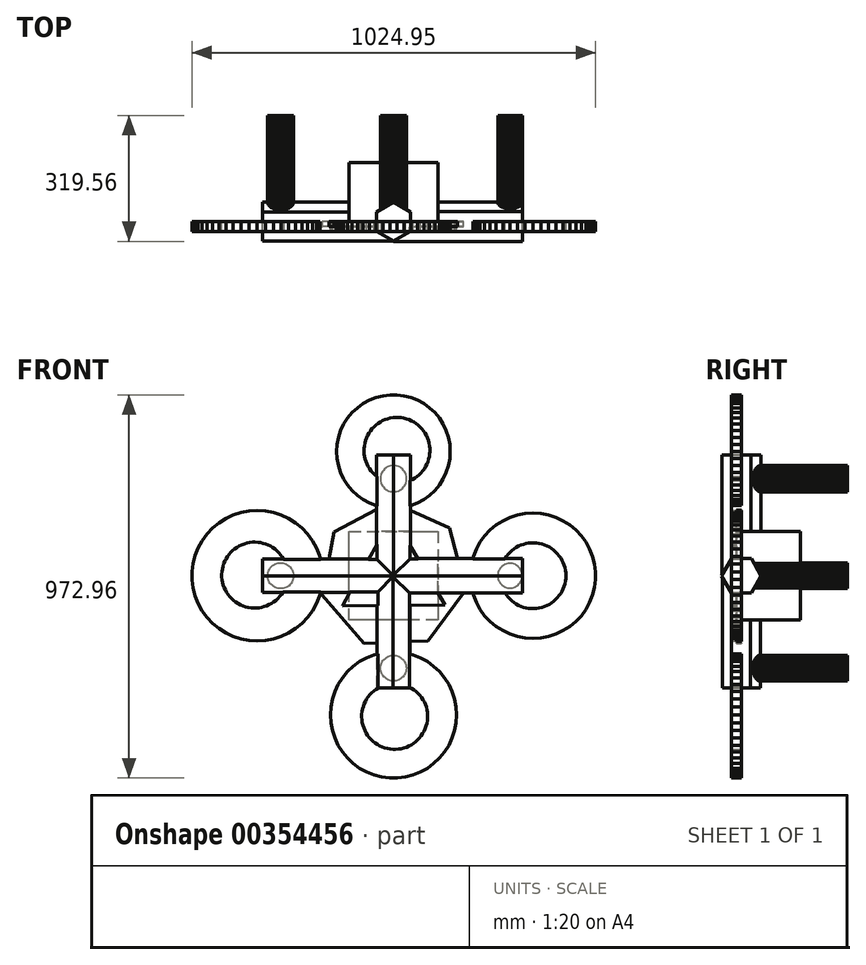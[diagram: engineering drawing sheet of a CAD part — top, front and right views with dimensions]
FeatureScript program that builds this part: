
annotation { "Feature Type Name" : "Feature", "Feature Type Description" : "" }
export const myFeature = defineFeature(function(context is Context, id is Id, definition is map)
    precondition{}
    {
        {
            var Q0;
            Q0=qCreatedBy(makeId("Front.planeOp"),FACE);
            var sketch = newSketch(context, id + "F0", { "sketchPlane" : qUnion([Q0])});
            skCircle(sketch, "E0.cCircle", {"center": v(0, 0) * mm, "radius": 75.35 * mm, "construction": true});
            skLineSegment(sketch, "E0.0", {"start": v(-129.73, -76.68) * mm, "end": v(-1.54, 150.7) * mm});
            skLineSegment(sketch, "E0.1", {"start": v(-1.54, 150.7) * mm, "end": v(131.28, -74.01) * mm});
            skLineSegment(sketch, "E0.2", {"start": v(131.28, -74.01) * mm, "end": v(-129.73, -76.68) * mm});
            skPoint(sketch, "E0.0.midPoint", {"position": v(-65.64, 37) * mm});
            skSolve(sketch);
        }
        {
            var Q0;
            Q0=makeQuery(id+"F0.imprint","IMPRINT",FACE,{"disambiguationData":[TD([[makeQuery(id+"F0.imprint","IMPRINT",EDGE,{"derivedFrom":sQuery(id+"F0.wireOp",EDGE,"E0.0")}),-1.0]])]});
            extrude(context, id + "F1", {"entities" : qUnion([Q0]), "depth" : 25.4 * mm});
        }
        {
            var Q0;
            Q0=qCreatedBy(makeId("Front.planeOp"),FACE);
            var sketch = newSketch(context, id + "F2", { "sketchPlane" : qUnion([Q0])});
            skCircle(sketch, "E1.cCircle", {"center": v(0, 0) * mm, "radius": 168.77 * mm, "construction": true});
            skLineSegment(sketch, "E1.0", {"start": v(-150.57, 111.44) * mm, "end": v(-6.75, 187.2) * mm});
            skLineSegment(sketch, "E1.1", {"start": v(-6.75, 187.2) * mm, "end": v(142.15, 122) * mm});
            skLineSegment(sketch, "E1.2", {"start": v(142.15, 122) * mm, "end": v(184.01, -35.08) * mm});
            skLineSegment(sketch, "E1.3", {"start": v(184.01, -35.08) * mm, "end": v(87.3, -165.74) * mm});
            skLineSegment(sketch, "E1.4", {"start": v(87.3, -165.74) * mm, "end": v(-75.14, -171.6) * mm});
            skLineSegment(sketch, "E1.5", {"start": v(-75.14, -171.6) * mm, "end": v(-181, -48.24) * mm});
            skLineSegment(sketch, "E1.6", {"start": v(-181, -48.24) * mm, "end": v(-150.57, 111.44) * mm});
            skPoint(sketch, "E1.0.midPoint", {"position": v(-78.66, 149.32) * mm});
            skSolve(sketch);
        }
        {
            var Q0;
            Q0=makeQuery(id+"F2.imprint","IMPRINT",FACE,{"disambiguationData":[TD([[makeQuery(id+"F2.imprint","IMPRINT",EDGE,{"derivedFrom":sQuery(id+"F2.wireOp",EDGE,"E1.0")}),-1.0]])]});
            extrude(context, id + "F3", {"entities" : qUnion([Q0]), "operationType" : NewBodyOperationType.ADD, "depth" : 12.95 * mm});
        }
        {
            var Q0;
            Q0=qCreatedBy(makeId("Right.planeOp"),FACE);
            var sketch = newSketch(context, id + "F4", { "sketchPlane" : qUnion([Q0])});
            skCircle(sketch, "E2.cCircle", {"center": v(0, 0) * mm, "radius": 43.58 * mm, "construction": true});
            skLineSegment(sketch, "E2.0", {"start": v(25.16, -43.58) * mm, "end": v(-25.16, -43.58) * mm});
            skLineSegment(sketch, "E2.1", {"start": v(-25.16, -43.58) * mm, "end": v(-50.32, 0) * mm});
            skLineSegment(sketch, "E2.2", {"start": v(-50.32, 0) * mm, "end": v(-25.16, 43.58) * mm});
            skLineSegment(sketch, "E2.3", {"start": v(-25.16, 43.58) * mm, "end": v(25.16, 43.58) * mm});
            skLineSegment(sketch, "E2.4", {"start": v(25.16, 43.58) * mm, "end": v(50.32, 0) * mm});
            skLineSegment(sketch, "E2.5", {"start": v(50.32, 0) * mm, "end": v(25.16, -43.58) * mm});
            skPoint(sketch, "E2.0.midPoint", {"position": v(0, -43.58) * mm});
            skSolve(sketch);
        }
        {
            var Q0;
            Q0 = qSketchRegion(id + "F4", true);
            extrude(context, id + "F5", {"entities" : qUnion([Q0]), "operationType" : NewBodyOperationType.ADD, "depth" : 327.66 * mm});
        }
        {
            var Q0;
            Q0=qCreatedBy(makeId("Right.planeOp"),FACE);
            var sketch = newSketch(context, id + "F6", { "sketchPlane" : qUnion([Q0])});
            skCircle(sketch, "E3.cCircle", {"center": v(0, 0) * mm, "radius": 42.73 * mm, "construction": true});
            skLineSegment(sketch, "E3.0", {"start": v(-49.35, 0.04) * mm, "end": v(-24.64, 42.76) * mm});
            skLineSegment(sketch, "E3.1", {"start": v(-24.64, 42.76) * mm, "end": v(24.7, 42.71) * mm});
            skLineSegment(sketch, "E3.2", {"start": v(24.7, 42.71) * mm, "end": v(49.35, -0.04) * mm});
            skLineSegment(sketch, "E3.3", {"start": v(49.35, -0.04) * mm, "end": v(24.64, -42.76) * mm});
            skLineSegment(sketch, "E3.4", {"start": v(24.64, -42.76) * mm, "end": v(-24.7, -42.71) * mm});
            skLineSegment(sketch, "E3.5", {"start": v(-24.7, -42.71) * mm, "end": v(-49.35, 0.04) * mm});
            skPoint(sketch, "E3.0.midPoint", {"position": v(-37, 21.4) * mm});
            skSolve(sketch);
        }
        {
            var Q0;
            Q0 = qSketchRegion(id + "F6", true);
            extrude(context, id + "F7", {"entities" : qUnion([Q0]), "operationType" : NewBodyOperationType.ADD, "oppositeDirection" : true, "depth" : 332.74 * mm});
        }
        {
            var Q0;
            Q0=qCreatedBy(makeId("Top.planeOp"),FACE);
            var sketch = newSketch(context, id + "F8", { "sketchPlane" : qUnion([Q0])});
            skCircle(sketch, "E4.cCircle", {"center": v(0, 0) * mm, "radius": 42.9 * mm, "construction": true});
            skLineSegment(sketch, "E4.0", {"start": v(-42.9, -24.77) * mm, "end": v(-42.9, 24.77) * mm});
            skLineSegment(sketch, "E4.1", {"start": v(-42.9, 24.77) * mm, "end": v(0, 49.53) * mm});
            skLineSegment(sketch, "E4.2", {"start": v(0, 49.53) * mm, "end": v(42.9, 24.77) * mm});
            skLineSegment(sketch, "E4.3", {"start": v(42.9, 24.77) * mm, "end": v(42.9, -24.77) * mm});
            skLineSegment(sketch, "E4.4", {"start": v(42.9, -24.77) * mm, "end": v(0, -49.53) * mm});
            skLineSegment(sketch, "E4.5", {"start": v(0, -49.53) * mm, "end": v(-42.9, -24.77) * mm});
            skPoint(sketch, "E4.0.midPoint", {"position": v(-42.9, 0) * mm});
            skSolve(sketch);
        }
        {
            var Q0;
            Q0 = qSketchRegion(id + "F8", true);
            extrude(context, id + "F9", {"entities" : qUnion([Q0]), "operationType" : NewBodyOperationType.ADD, "depth" : 307.34 * mm});
        }
        {
            var Q0;
            Q0=qCreatedBy(makeId("Top.planeOp"),FACE);
            var sketch = newSketch(context, id + "F10", { "sketchPlane" : qUnion([Q0])});
            skCircle(sketch, "E5.cCircle", {"center": v(0, 0) * mm, "radius": 41.69 * mm, "construction": true});
            skLineSegment(sketch, "E5.0", {"start": v(-0.86, -48.13) * mm, "end": v(-42.11, -23.32) * mm});
            skLineSegment(sketch, "E5.1", {"start": v(-42.11, -23.32) * mm, "end": v(-41.25, 24.81) * mm});
            skLineSegment(sketch, "E5.2", {"start": v(-41.25, 24.81) * mm, "end": v(0.86, 48.13) * mm});
            skLineSegment(sketch, "E5.3", {"start": v(0.86, 48.13) * mm, "end": v(42.11, 23.32) * mm});
            skLineSegment(sketch, "E5.4", {"start": v(42.11, 23.32) * mm, "end": v(41.25, -24.81) * mm});
            skLineSegment(sketch, "E5.5", {"start": v(41.25, -24.81) * mm, "end": v(-0.86, -48.13) * mm});
            skPoint(sketch, "E5.0.midPoint", {"position": v(-21.49, -35.72) * mm});
            skSolve(sketch);
        }
        {
            var Q0;
            Q0 = qSketchRegion(id + "F10", true);
            extrude(context, id + "F11", {"entities" : qUnion([Q0]), "operationType" : NewBodyOperationType.ADD, "oppositeDirection" : true, "depth" : 284.48 * mm});
        }
        {
            var Q0;
            Q0=qCreatedBy(makeId("Front.planeOp"),FACE);
            var sketch = newSketch(context, id + "F12", { "sketchPlane" : qUnion([Q0])});
            skCircle(sketch, "E6.cCircle", {"center": v(0, 315.57) * mm, "radius": 143.82 * mm, "construction": true});
            skLineSegment(sketch, "E6.0", {"start": v(-9.05, 459.4) * mm, "end": v(9.05, 459.4) * mm});
            skLineSegment(sketch, "E6.1", {"start": v(9.05, 459.4) * mm, "end": v(27, 457.13) * mm});
            skLineSegment(sketch, "E6.2", {"start": v(27, 457.13) * mm, "end": v(44.53, 452.63) * mm});
            skLineSegment(sketch, "E6.3", {"start": v(44.53, 452.63) * mm, "end": v(61.36, 445.96) * mm});
            skLineSegment(sketch, "E6.4", {"start": v(61.36, 445.96) * mm, "end": v(77.22, 437.25) * mm});
            skLineSegment(sketch, "E6.5", {"start": v(77.22, 437.25) * mm, "end": v(91.86, 426.6) * mm});
            skLineSegment(sketch, "E6.6", {"start": v(91.86, 426.6) * mm, "end": v(105.05, 414.22) * mm});
            skLineSegment(sketch, "E6.7", {"start": v(105.05, 414.22) * mm, "end": v(116.58, 400.28) * mm});
            skLineSegment(sketch, "E6.8", {"start": v(116.58, 400.28) * mm, "end": v(126.28, 385) * mm});
            skLineSegment(sketch, "E6.9", {"start": v(126.28, 385) * mm, "end": v(133.99, 368.62) * mm});
            skLineSegment(sketch, "E6.10", {"start": v(133.99, 368.62) * mm, "end": v(139.58, 351.41) * mm});
            skLineSegment(sketch, "E6.11", {"start": v(139.58, 351.41) * mm, "end": v(142.97, 333.63) * mm});
            skLineSegment(sketch, "E6.12", {"start": v(142.97, 333.63) * mm, "end": v(144.1, 315.57) * mm});
            skLineSegment(sketch, "E6.13", {"start": v(144.1, 315.57) * mm, "end": v(142.97, 297.51) * mm});
            skLineSegment(sketch, "E6.14", {"start": v(142.97, 297.51) * mm, "end": v(139.58, 279.74) * mm});
            skLineSegment(sketch, "E6.15", {"start": v(139.58, 279.74) * mm, "end": v(133.99, 262.52) * mm});
            skLineSegment(sketch, "E6.16", {"start": v(133.99, 262.52) * mm, "end": v(126.28, 246.15) * mm});
            skLineSegment(sketch, "E6.17", {"start": v(126.28, 246.15) * mm, "end": v(116.58, 230.87) * mm});
            skLineSegment(sketch, "E6.18", {"start": v(116.58, 230.87) * mm, "end": v(105.05, 216.93) * mm});
            skLineSegment(sketch, "E6.19", {"start": v(105.05, 216.93) * mm, "end": v(91.86, 204.54) * mm});
            skLineSegment(sketch, "E6.20", {"start": v(91.86, 204.54) * mm, "end": v(77.22, 193.9) * mm});
            skLineSegment(sketch, "E6.21", {"start": v(77.22, 193.9) * mm, "end": v(61.36, 185.18) * mm});
            skLineSegment(sketch, "E6.22", {"start": v(61.36, 185.18) * mm, "end": v(44.53, 178.52) * mm});
            skLineSegment(sketch, "E6.23", {"start": v(44.53, 178.52) * mm, "end": v(27, 174.02) * mm});
            skLineSegment(sketch, "E6.24", {"start": v(27, 174.02) * mm, "end": v(9.05, 171.75) * mm});
            skLineSegment(sketch, "E6.25", {"start": v(9.05, 171.75) * mm, "end": v(-9.05, 171.75) * mm});
            skLineSegment(sketch, "E6.26", {"start": v(-9.05, 171.75) * mm, "end": v(-27, 174.02) * mm});
            skLineSegment(sketch, "E6.27", {"start": v(-27, 174.02) * mm, "end": v(-44.53, 178.52) * mm});
            skLineSegment(sketch, "E6.28", {"start": v(-44.53, 178.52) * mm, "end": v(-61.36, 185.18) * mm});
            skLineSegment(sketch, "E6.29", {"start": v(-61.36, 185.18) * mm, "end": v(-77.22, 193.9) * mm});
            skLineSegment(sketch, "E6.30", {"start": v(-77.22, 193.9) * mm, "end": v(-91.86, 204.54) * mm});
            skLineSegment(sketch, "E6.31", {"start": v(-91.86, 204.54) * mm, "end": v(-105.05, 216.93) * mm});
            skLineSegment(sketch, "E6.32", {"start": v(-105.05, 216.93) * mm, "end": v(-116.58, 230.87) * mm});
            skLineSegment(sketch, "E6.33", {"start": v(-116.58, 230.87) * mm, "end": v(-126.28, 246.15) * mm});
            skLineSegment(sketch, "E6.34", {"start": v(-126.28, 246.15) * mm, "end": v(-133.99, 262.52) * mm});
            skLineSegment(sketch, "E6.35", {"start": v(-133.99, 262.52) * mm, "end": v(-139.58, 279.74) * mm});
            skLineSegment(sketch, "E6.36", {"start": v(-139.58, 279.74) * mm, "end": v(-142.97, 297.51) * mm});
            skLineSegment(sketch, "E6.37", {"start": v(-142.97, 297.51) * mm, "end": v(-144.1, 315.57) * mm});
            skLineSegment(sketch, "E6.38", {"start": v(-144.1, 315.57) * mm, "end": v(-142.97, 333.63) * mm});
            skLineSegment(sketch, "E6.39", {"start": v(-142.97, 333.63) * mm, "end": v(-139.58, 351.41) * mm});
            skLineSegment(sketch, "E6.40", {"start": v(-139.58, 351.41) * mm, "end": v(-133.99, 368.62) * mm});
            skLineSegment(sketch, "E6.41", {"start": v(-133.99, 368.62) * mm, "end": v(-126.28, 385) * mm});
            skLineSegment(sketch, "E6.42", {"start": v(-126.28, 385) * mm, "end": v(-116.58, 400.28) * mm});
            skLineSegment(sketch, "E6.43", {"start": v(-116.58, 400.28) * mm, "end": v(-105.05, 414.22) * mm});
            skLineSegment(sketch, "E6.44", {"start": v(-105.05, 414.22) * mm, "end": v(-91.86, 426.6) * mm});
            skLineSegment(sketch, "E6.45", {"start": v(-91.86, 426.6) * mm, "end": v(-77.22, 437.25) * mm});
            skLineSegment(sketch, "E6.46", {"start": v(-77.22, 437.25) * mm, "end": v(-61.36, 445.96) * mm});
            skLineSegment(sketch, "E6.47", {"start": v(-61.36, 445.96) * mm, "end": v(-44.53, 452.63) * mm});
            skLineSegment(sketch, "E6.48", {"start": v(-44.53, 452.63) * mm, "end": v(-27, 457.13) * mm});
            skLineSegment(sketch, "E6.49", {"start": v(-27, 457.13) * mm, "end": v(-9.05, 459.4) * mm});
            skPoint(sketch, "E6.0.midPoint", {"position": v(0, 459.4) * mm});
            skCircle(sketch, "E7.cCircle", {"center": v(354.48, 0) * mm, "radius": 158.96 * mm, "construction": true});
            skLineSegment(sketch, "E7.0", {"start": v(513.44, 10) * mm, "end": v(513.44, -10) * mm});
            skLineSegment(sketch, "E7.1", {"start": v(513.44, -10) * mm, "end": v(510.94, -29.85) * mm});
            skLineSegment(sketch, "E7.2", {"start": v(510.94, -29.85) * mm, "end": v(505.96, -49.22) * mm});
            skLineSegment(sketch, "E7.3", {"start": v(505.96, -49.22) * mm, "end": v(498.6, -67.82) * mm});
            skLineSegment(sketch, "E7.4", {"start": v(498.6, -67.82) * mm, "end": v(488.96, -85.34) * mm});
            skLineSegment(sketch, "E7.5", {"start": v(488.96, -85.34) * mm, "end": v(477.2, -101.53) * mm});
            skLineSegment(sketch, "E7.6", {"start": v(477.2, -101.53) * mm, "end": v(463.51, -116.1) * mm});
            skLineSegment(sketch, "E7.7", {"start": v(463.51, -116.1) * mm, "end": v(448.1, -128.86) * mm});
            skLineSegment(sketch, "E7.8", {"start": v(448.1, -128.86) * mm, "end": v(431.21, -139.57) * mm});
            skLineSegment(sketch, "E7.9", {"start": v(431.21, -139.57) * mm, "end": v(413.12, -148.1) * mm});
            skLineSegment(sketch, "E7.10", {"start": v(413.12, -148.1) * mm, "end": v(394.1, -154.27) * mm});
            skLineSegment(sketch, "E7.11", {"start": v(394.1, -154.27) * mm, "end": v(374.44, -158.02) * mm});
            skLineSegment(sketch, "E7.12", {"start": v(374.44, -158.02) * mm, "end": v(354.48, -159.28) * mm});
            skLineSegment(sketch, "E7.13", {"start": v(354.48, -159.28) * mm, "end": v(334.52, -158.02) * mm});
            skLineSegment(sketch, "E7.14", {"start": v(334.52, -158.02) * mm, "end": v(314.87, -154.27) * mm});
            skLineSegment(sketch, "E7.15", {"start": v(314.87, -154.27) * mm, "end": v(295.85, -148.1) * mm});
            skLineSegment(sketch, "E7.16", {"start": v(295.85, -148.1) * mm, "end": v(277.75, -139.57) * mm});
            skLineSegment(sketch, "E7.17", {"start": v(277.75, -139.57) * mm, "end": v(260.86, -128.86) * mm});
            skLineSegment(sketch, "E7.18", {"start": v(260.86, -128.86) * mm, "end": v(245.45, -116.1) * mm});
            skLineSegment(sketch, "E7.19", {"start": v(245.45, -116.1) * mm, "end": v(231.76, -101.53) * mm});
            skLineSegment(sketch, "E7.20", {"start": v(231.76, -101.53) * mm, "end": v(220, -85.34) * mm});
            skLineSegment(sketch, "E7.21", {"start": v(220, -85.34) * mm, "end": v(210.36, -67.82) * mm});
            skLineSegment(sketch, "E7.22", {"start": v(210.36, -67.82) * mm, "end": v(203, -49.22) * mm});
            skLineSegment(sketch, "E7.23", {"start": v(203, -49.22) * mm, "end": v(198.03, -29.85) * mm});
            skLineSegment(sketch, "E7.24", {"start": v(198.03, -29.85) * mm, "end": v(195.52, -10) * mm});
            skLineSegment(sketch, "E7.25", {"start": v(195.52, -10) * mm, "end": v(195.52, 10) * mm});
            skLineSegment(sketch, "E7.26", {"start": v(195.52, 10) * mm, "end": v(198.03, 29.85) * mm});
            skLineSegment(sketch, "E7.27", {"start": v(198.03, 29.85) * mm, "end": v(203, 49.22) * mm});
            skLineSegment(sketch, "E7.28", {"start": v(203, 49.22) * mm, "end": v(210.36, 67.82) * mm});
            skLineSegment(sketch, "E7.29", {"start": v(210.36, 67.82) * mm, "end": v(220, 85.34) * mm});
            skLineSegment(sketch, "E7.30", {"start": v(220, 85.34) * mm, "end": v(231.76, 101.53) * mm});
            skLineSegment(sketch, "E7.31", {"start": v(231.76, 101.53) * mm, "end": v(245.45, 116.1) * mm});
            skLineSegment(sketch, "E7.32", {"start": v(245.45, 116.1) * mm, "end": v(260.86, 128.86) * mm});
            skLineSegment(sketch, "E7.33", {"start": v(260.86, 128.86) * mm, "end": v(277.75, 139.57) * mm});
            skLineSegment(sketch, "E7.34", {"start": v(277.75, 139.57) * mm, "end": v(295.85, 148.1) * mm});
            skLineSegment(sketch, "E7.35", {"start": v(295.85, 148.1) * mm, "end": v(314.87, 154.27) * mm});
            skLineSegment(sketch, "E7.36", {"start": v(314.87, 154.27) * mm, "end": v(334.52, 158.02) * mm});
            skLineSegment(sketch, "E7.37", {"start": v(334.52, 158.02) * mm, "end": v(354.48, 159.28) * mm});
            skLineSegment(sketch, "E7.38", {"start": v(354.48, 159.28) * mm, "end": v(374.44, 158.02) * mm});
            skLineSegment(sketch, "E7.39", {"start": v(374.44, 158.02) * mm, "end": v(394.1, 154.27) * mm});
            skLineSegment(sketch, "E7.40", {"start": v(394.1, 154.27) * mm, "end": v(413.12, 148.1) * mm});
            skLineSegment(sketch, "E7.41", {"start": v(413.12, 148.1) * mm, "end": v(431.21, 139.57) * mm});
            skLineSegment(sketch, "E7.42", {"start": v(431.21, 139.57) * mm, "end": v(448.1, 128.86) * mm});
            skLineSegment(sketch, "E7.43", {"start": v(448.1, 128.86) * mm, "end": v(463.51, 116.1) * mm});
            skLineSegment(sketch, "E7.44", {"start": v(463.51, 116.1) * mm, "end": v(477.2, 101.53) * mm});
            skLineSegment(sketch, "E7.45", {"start": v(477.2, 101.53) * mm, "end": v(488.96, 85.34) * mm});
            skLineSegment(sketch, "E7.46", {"start": v(488.96, 85.34) * mm, "end": v(498.6, 67.82) * mm});
            skLineSegment(sketch, "E7.47", {"start": v(498.6, 67.82) * mm, "end": v(505.96, 49.22) * mm});
            skLineSegment(sketch, "E7.48", {"start": v(505.96, 49.22) * mm, "end": v(510.94, 29.85) * mm});
            skLineSegment(sketch, "E7.49", {"start": v(510.94, 29.85) * mm, "end": v(513.44, 10) * mm});
            skPoint(sketch, "E7.0.midPoint", {"position": v(513.44, 0) * mm});
            skCircle(sketch, "E8.cCircle", {"center": v(-346.01, 0) * mm, "radius": 165.5 * mm, "construction": true});
            skLineSegment(sketch, "E8.0", {"start": v(-511.5, -10.41) * mm, "end": v(-511.5, 10.41) * mm});
            skLineSegment(sketch, "E8.1", {"start": v(-511.5, 10.41) * mm, "end": v(-508.9, 31.07) * mm});
            skLineSegment(sketch, "E8.2", {"start": v(-508.9, 31.07) * mm, "end": v(-503.72, 51.24) * mm});
            skLineSegment(sketch, "E8.3", {"start": v(-503.72, 51.24) * mm, "end": v(-496.05, 70.6) * mm});
            skLineSegment(sketch, "E8.4", {"start": v(-496.05, 70.6) * mm, "end": v(-486.02, 88.85) * mm});
            skLineSegment(sketch, "E8.5", {"start": v(-486.02, 88.85) * mm, "end": v(-473.78, 105.7) * mm});
            skLineSegment(sketch, "E8.6", {"start": v(-473.78, 105.7) * mm, "end": v(-459.53, 120.88) * mm});
            skLineSegment(sketch, "E8.7", {"start": v(-459.53, 120.88) * mm, "end": v(-443.48, 134.15) * mm});
            skLineSegment(sketch, "E8.8", {"start": v(-443.48, 134.15) * mm, "end": v(-425.9, 145.31) * mm});
            skLineSegment(sketch, "E8.9", {"start": v(-425.9, 145.31) * mm, "end": v(-407.06, 154.18) * mm});
            skLineSegment(sketch, "E8.10", {"start": v(-407.06, 154.18) * mm, "end": v(-387.25, 160.61) * mm});
            skLineSegment(sketch, "E8.11", {"start": v(-387.25, 160.61) * mm, "end": v(-366.8, 164.52) * mm});
            skLineSegment(sketch, "E8.12", {"start": v(-366.8, 164.52) * mm, "end": v(-346.01, 165.82) * mm});
            skLineSegment(sketch, "E8.13", {"start": v(-346.01, 165.82) * mm, "end": v(-325.23, 164.52) * mm});
            skLineSegment(sketch, "E8.14", {"start": v(-325.23, 164.52) * mm, "end": v(-304.78, 160.61) * mm});
            skLineSegment(sketch, "E8.15", {"start": v(-304.78, 160.61) * mm, "end": v(-284.97, 154.18) * mm});
            skLineSegment(sketch, "E8.16", {"start": v(-284.97, 154.18) * mm, "end": v(-266.13, 145.31) * mm});
            skLineSegment(sketch, "E8.17", {"start": v(-266.13, 145.31) * mm, "end": v(-248.55, 134.15) * mm});
            skLineSegment(sketch, "E8.18", {"start": v(-248.55, 134.15) * mm, "end": v(-232.5, 120.88) * mm});
            skLineSegment(sketch, "E8.19", {"start": v(-232.5, 120.88) * mm, "end": v(-218.25, 105.7) * mm});
            skLineSegment(sketch, "E8.20", {"start": v(-218.25, 105.7) * mm, "end": v(-206, 88.85) * mm});
            skLineSegment(sketch, "E8.21", {"start": v(-206, 88.85) * mm, "end": v(-195.97, 70.6) * mm});
            skLineSegment(sketch, "E8.22", {"start": v(-195.97, 70.6) * mm, "end": v(-188.3, 51.24) * mm});
            skLineSegment(sketch, "E8.23", {"start": v(-188.3, 51.24) * mm, "end": v(-183.13, 31.07) * mm});
            skLineSegment(sketch, "E8.24", {"start": v(-183.13, 31.07) * mm, "end": v(-180.52, 10.41) * mm});
            skLineSegment(sketch, "E8.25", {"start": v(-180.52, 10.41) * mm, "end": v(-180.52, -10.41) * mm});
            skLineSegment(sketch, "E8.26", {"start": v(-180.52, -10.41) * mm, "end": v(-183.13, -31.07) * mm});
            skLineSegment(sketch, "E8.27", {"start": v(-183.13, -31.07) * mm, "end": v(-188.3, -51.24) * mm});
            skLineSegment(sketch, "E8.28", {"start": v(-188.3, -51.24) * mm, "end": v(-195.97, -70.6) * mm});
            skLineSegment(sketch, "E8.29", {"start": v(-195.97, -70.6) * mm, "end": v(-206, -88.85) * mm});
            skLineSegment(sketch, "E8.30", {"start": v(-206, -88.85) * mm, "end": v(-218.25, -105.7) * mm});
            skLineSegment(sketch, "E8.31", {"start": v(-218.25, -105.7) * mm, "end": v(-232.5, -120.88) * mm});
            skLineSegment(sketch, "E8.32", {"start": v(-232.5, -120.88) * mm, "end": v(-248.55, -134.15) * mm});
            skLineSegment(sketch, "E8.33", {"start": v(-248.55, -134.15) * mm, "end": v(-266.13, -145.31) * mm});
            skLineSegment(sketch, "E8.34", {"start": v(-266.13, -145.31) * mm, "end": v(-284.97, -154.18) * mm});
            skLineSegment(sketch, "E8.35", {"start": v(-284.97, -154.18) * mm, "end": v(-304.78, -160.61) * mm});
            skLineSegment(sketch, "E8.36", {"start": v(-304.78, -160.61) * mm, "end": v(-325.23, -164.52) * mm});
            skLineSegment(sketch, "E8.37", {"start": v(-325.23, -164.52) * mm, "end": v(-346.01, -165.82) * mm});
            skLineSegment(sketch, "E8.38", {"start": v(-346.01, -165.82) * mm, "end": v(-366.8, -164.52) * mm});
            skLineSegment(sketch, "E8.39", {"start": v(-366.8, -164.52) * mm, "end": v(-387.25, -160.61) * mm});
            skLineSegment(sketch, "E8.40", {"start": v(-387.25, -160.61) * mm, "end": v(-407.06, -154.18) * mm});
            skLineSegment(sketch, "E8.41", {"start": v(-407.06, -154.18) * mm, "end": v(-425.9, -145.31) * mm});
            skLineSegment(sketch, "E8.42", {"start": v(-425.9, -145.31) * mm, "end": v(-443.48, -134.15) * mm});
            skLineSegment(sketch, "E8.43", {"start": v(-443.48, -134.15) * mm, "end": v(-459.53, -120.88) * mm});
            skLineSegment(sketch, "E8.44", {"start": v(-459.53, -120.88) * mm, "end": v(-473.78, -105.7) * mm});
            skLineSegment(sketch, "E8.45", {"start": v(-473.78, -105.7) * mm, "end": v(-486.02, -88.85) * mm});
            skLineSegment(sketch, "E8.46", {"start": v(-486.02, -88.85) * mm, "end": v(-496.05, -70.6) * mm});
            skLineSegment(sketch, "E8.47", {"start": v(-496.05, -70.6) * mm, "end": v(-503.72, -51.24) * mm});
            skLineSegment(sketch, "E8.48", {"start": v(-503.72, -51.24) * mm, "end": v(-508.9, -31.07) * mm});
            skLineSegment(sketch, "E8.49", {"start": v(-508.9, -31.07) * mm, "end": v(-511.5, -10.41) * mm});
            skPoint(sketch, "E8.0.midPoint", {"position": v(-511.5, 0) * mm});
            skCircle(sketch, "E9", {"center": v(354.48, 0) * mm, "radius": 83.72 * mm});
            skCircle(sketch, "E10", {"center": v(8.9, 318.44) * mm, "radius": 83.72 * mm});
            skCircle(sketch, "E11", {"center": v(-352.54, 1.62) * mm, "radius": 83.72 * mm});
            skSolve(sketch);
        }
        {
            var Q0;
            Q0=qCreatedBy(makeId("Front.planeOp"),FACE);
            var sketch = newSketch(context, id + "F13", { "sketchPlane" : qUnion([Q0])});
            skCircle(sketch, "E12.cCircle", {"center": v(0, -353.48) * mm, "radius": 160.08 * mm, "construction": true});
            skLineSegment(sketch, "E12.0", {"start": v(-10.07, -193.4) * mm, "end": v(10.07, -193.4) * mm});
            skLineSegment(sketch, "E12.1", {"start": v(10.07, -193.4) * mm, "end": v(30.05, -195.93) * mm});
            skLineSegment(sketch, "E12.2", {"start": v(30.05, -195.93) * mm, "end": v(49.56, -200.94) * mm});
            skLineSegment(sketch, "E12.3", {"start": v(49.56, -200.94) * mm, "end": v(68.3, -208.35) * mm});
            skLineSegment(sketch, "E12.4", {"start": v(68.3, -208.35) * mm, "end": v(85.94, -218.06) * mm});
            skLineSegment(sketch, "E12.5", {"start": v(85.94, -218.06) * mm, "end": v(102.24, -229.9) * mm});
            skLineSegment(sketch, "E12.6", {"start": v(102.24, -229.9) * mm, "end": v(116.92, -243.69) * mm});
            skLineSegment(sketch, "E12.7", {"start": v(116.92, -243.69) * mm, "end": v(129.76, -259.2) * mm});
            skLineSegment(sketch, "E12.8", {"start": v(129.76, -259.2) * mm, "end": v(140.55, -276.21) * mm});
            skLineSegment(sketch, "E12.9", {"start": v(140.55, -276.21) * mm, "end": v(149.13, -294.44) * mm});
            skLineSegment(sketch, "E12.10", {"start": v(149.13, -294.44) * mm, "end": v(155.35, -313.6) * mm});
            skLineSegment(sketch, "E12.11", {"start": v(155.35, -313.6) * mm, "end": v(159.13, -333.38) * mm});
            skLineSegment(sketch, "E12.12", {"start": v(159.13, -333.38) * mm, "end": v(160.4, -353.48) * mm});
            skLineSegment(sketch, "E12.13", {"start": v(160.4, -353.48) * mm, "end": v(159.13, -373.58) * mm});
            skLineSegment(sketch, "E12.14", {"start": v(159.13, -373.58) * mm, "end": v(155.35, -393.37) * mm});
            skLineSegment(sketch, "E12.15", {"start": v(155.35, -393.37) * mm, "end": v(149.13, -412.53) * mm});
            skLineSegment(sketch, "E12.16", {"start": v(149.13, -412.53) * mm, "end": v(140.55, -430.75) * mm});
            skLineSegment(sketch, "E12.17", {"start": v(140.55, -430.75) * mm, "end": v(129.76, -447.76) * mm});
            skLineSegment(sketch, "E12.18", {"start": v(129.76, -447.76) * mm, "end": v(116.92, -463.28) * mm});
            skLineSegment(sketch, "E12.19", {"start": v(116.92, -463.28) * mm, "end": v(102.24, -477.07) * mm});
            skLineSegment(sketch, "E12.20", {"start": v(102.24, -477.07) * mm, "end": v(85.94, -488.9) * mm});
            skLineSegment(sketch, "E12.21", {"start": v(85.94, -488.9) * mm, "end": v(68.3, -498.6) * mm});
            skLineSegment(sketch, "E12.22", {"start": v(68.3, -498.6) * mm, "end": v(49.56, -506.02) * mm});
            skLineSegment(sketch, "E12.23", {"start": v(49.56, -506.02) * mm, "end": v(30.05, -511.03) * mm});
            skLineSegment(sketch, "E12.24", {"start": v(30.05, -511.03) * mm, "end": v(10.07, -513.56) * mm});
            skLineSegment(sketch, "E12.25", {"start": v(10.07, -513.56) * mm, "end": v(-10.07, -513.56) * mm});
            skLineSegment(sketch, "E12.26", {"start": v(-10.07, -513.56) * mm, "end": v(-30.05, -511.03) * mm});
            skLineSegment(sketch, "E12.27", {"start": v(-30.05, -511.03) * mm, "end": v(-49.56, -506.02) * mm});
            skLineSegment(sketch, "E12.28", {"start": v(-49.56, -506.02) * mm, "end": v(-68.3, -498.6) * mm});
            skLineSegment(sketch, "E12.29", {"start": v(-68.3, -498.6) * mm, "end": v(-85.94, -488.9) * mm});
            skLineSegment(sketch, "E12.30", {"start": v(-85.94, -488.9) * mm, "end": v(-102.24, -477.07) * mm});
            skLineSegment(sketch, "E12.31", {"start": v(-102.24, -477.07) * mm, "end": v(-116.92, -463.28) * mm});
            skLineSegment(sketch, "E12.32", {"start": v(-116.92, -463.28) * mm, "end": v(-129.76, -447.76) * mm});
            skLineSegment(sketch, "E12.33", {"start": v(-129.76, -447.76) * mm, "end": v(-140.55, -430.75) * mm});
            skLineSegment(sketch, "E12.34", {"start": v(-140.55, -430.75) * mm, "end": v(-149.13, -412.53) * mm});
            skLineSegment(sketch, "E12.35", {"start": v(-149.13, -412.53) * mm, "end": v(-155.35, -393.37) * mm});
            skLineSegment(sketch, "E12.36", {"start": v(-155.35, -393.37) * mm, "end": v(-159.13, -373.58) * mm});
            skLineSegment(sketch, "E12.37", {"start": v(-159.13, -373.58) * mm, "end": v(-160.4, -353.48) * mm});
            skLineSegment(sketch, "E12.38", {"start": v(-160.4, -353.48) * mm, "end": v(-159.13, -333.38) * mm});
            skLineSegment(sketch, "E12.39", {"start": v(-159.13, -333.38) * mm, "end": v(-155.35, -313.6) * mm});
            skLineSegment(sketch, "E12.40", {"start": v(-155.35, -313.6) * mm, "end": v(-149.13, -294.44) * mm});
            skLineSegment(sketch, "E12.41", {"start": v(-149.13, -294.44) * mm, "end": v(-140.55, -276.21) * mm});
            skLineSegment(sketch, "E12.42", {"start": v(-140.55, -276.21) * mm, "end": v(-129.76, -259.2) * mm});
            skLineSegment(sketch, "E12.43", {"start": v(-129.76, -259.2) * mm, "end": v(-116.92, -243.69) * mm});
            skLineSegment(sketch, "E12.44", {"start": v(-116.92, -243.69) * mm, "end": v(-102.24, -229.9) * mm});
            skLineSegment(sketch, "E12.45", {"start": v(-102.24, -229.9) * mm, "end": v(-85.94, -218.06) * mm});
            skLineSegment(sketch, "E12.46", {"start": v(-85.94, -218.06) * mm, "end": v(-68.3, -208.35) * mm});
            skLineSegment(sketch, "E12.47", {"start": v(-68.3, -208.35) * mm, "end": v(-49.56, -200.94) * mm});
            skLineSegment(sketch, "E12.48", {"start": v(-49.56, -200.94) * mm, "end": v(-30.05, -195.93) * mm});
            skLineSegment(sketch, "E12.49", {"start": v(-30.05, -195.93) * mm, "end": v(-10.07, -193.4) * mm});
            skPoint(sketch, "E12.0.midPoint", {"position": v(0, -193.4) * mm});
            skCircle(sketch, "E13", {"center": v(3.04, -357.32) * mm, "radius": 83.72 * mm});
            skSolve(sketch);
        }
        {
            var Q0;
            Q0 = qSketchRegion(id + "F12", true);
            extrude(context, id + "F14", {"entities" : qUnion([Q0]), "operationType" : NewBodyOperationType.ADD, "depth" : 25.4 * mm});
        }
        {
            var Q0;
            Q0=makeQuery(id+"F13.imprint","IMPRINT",FACE,{"disambiguationData":[TD([[makeQuery(id+"F13.imprint","IMPRINT",EDGE,{"derivedFrom":sQuery(id+"F13.wireOp",EDGE,"E12.0")}),-1.0]])]});
            extrude(context, id + "F15", {"entities" : qUnion([Q0]), "operationType" : NewBodyOperationType.ADD, "depth" : 25.4 * mm});
        }
        {
            var Q0;
            Q0=qCreatedBy(makeId("Front.planeOp"),FACE);
            var sketch = newSketch(context, id + "F16", { "sketchPlane" : qUnion([Q0])});
            skCircle(sketch, "E14.cCircle", {"center": v(0, 0) * mm, "radius": 112.76 * mm, "construction": true});
            skLineSegment(sketch, "E14.0", {"start": v(-112.76, 112.76) * mm, "end": v(112.76, 112.76) * mm});
            skLineSegment(sketch, "E14.1", {"start": v(112.76, 112.76) * mm, "end": v(112.76, -112.76) * mm});
            skLineSegment(sketch, "E14.2", {"start": v(112.76, -112.76) * mm, "end": v(-112.76, -112.76) * mm});
            skLineSegment(sketch, "E14.3", {"start": v(-112.76, -112.76) * mm, "end": v(-112.76, 112.76) * mm});
            skPoint(sketch, "E14.0.midPoint", {"position": v(0, 112.76) * mm});
            skSolve(sketch);
        }
        {
            var Q0;
            Q0 = qSketchRegion(id + "F16", true);
            extrude(context, id + "F17", {"entities" : qUnion([Q0]), "operationType" : NewBodyOperationType.ADD, "oppositeDirection" : true, "depth" : 149.86 * mm});
        }
        {
            var Q0;
            Q0=qCreatedBy(makeId("Front.planeOp"),FACE);
            var sketch = newSketch(context, id + "F18", { "sketchPlane" : qUnion([Q0])});
            skCircle(sketch, "E15.cCircle", {"center": v(296.11, 0) * mm, "radius": 31.12 * mm, "construction": true});
            skLineSegment(sketch, "E15.0", {"start": v(312.89, 26.28) * mm, "end": v(316.05, 23.98) * mm});
            skLineSegment(sketch, "E15.1", {"start": v(316.05, 23.98) * mm, "end": v(318.9, 21.29) * mm});
            skLineSegment(sketch, "E15.2", {"start": v(318.9, 21.29) * mm, "end": v(321.39, 18.26) * mm});
            skLineSegment(sketch, "E15.3", {"start": v(321.39, 18.26) * mm, "end": v(323.47, 14.95) * mm});
            skLineSegment(sketch, "E15.4", {"start": v(323.47, 14.95) * mm, "end": v(325.13, 11.4) * mm});
            skLineSegment(sketch, "E15.5", {"start": v(325.13, 11.4) * mm, "end": v(326.33, 7.68) * mm});
            skLineSegment(sketch, "E15.6", {"start": v(326.33, 7.68) * mm, "end": v(327.06, 3.83) * mm});
            skLineSegment(sketch, "E15.7", {"start": v(327.06, 3.83) * mm, "end": v(327.3, -0.08) * mm});
            skLineSegment(sketch, "E15.8", {"start": v(327.3, -0.08) * mm, "end": v(327.04, -3.99) * mm});
            skLineSegment(sketch, "E15.9", {"start": v(327.04, -3.99) * mm, "end": v(326.3, -7.83) * mm});
            skLineSegment(sketch, "E15.10", {"start": v(326.3, -7.83) * mm, "end": v(325.07, -11.55) * mm});
            skLineSegment(sketch, "E15.11", {"start": v(325.07, -11.55) * mm, "end": v(323.4, -15.1) * mm});
            skLineSegment(sketch, "E15.12", {"start": v(323.4, -15.1) * mm, "end": v(321.3, -18.4) * mm});
            skLineSegment(sketch, "E15.13", {"start": v(321.3, -18.4) * mm, "end": v(318.79, -21.4) * mm});
            skLineSegment(sketch, "E15.14", {"start": v(318.79, -21.4) * mm, "end": v(315.93, -24.08) * mm});
            skLineSegment(sketch, "E15.15", {"start": v(315.93, -24.08) * mm, "end": v(312.75, -26.37) * mm});
            skLineSegment(sketch, "E15.16", {"start": v(312.75, -26.37) * mm, "end": v(309.32, -28.25) * mm});
            skLineSegment(sketch, "E15.17", {"start": v(309.32, -28.25) * mm, "end": v(305.67, -29.68) * mm});
            skLineSegment(sketch, "E15.18", {"start": v(305.67, -29.68) * mm, "end": v(301.88, -30.64) * mm});
            skLineSegment(sketch, "E15.19", {"start": v(301.88, -30.64) * mm, "end": v(298, -31.12) * mm});
            skLineSegment(sketch, "E15.20", {"start": v(298, -31.12) * mm, "end": v(294.08, -31.11) * mm});
            skLineSegment(sketch, "E15.21", {"start": v(294.08, -31.11) * mm, "end": v(290.2, -30.61) * mm});
            skLineSegment(sketch, "E15.22", {"start": v(290.2, -30.61) * mm, "end": v(286.4, -29.63) * mm});
            skLineSegment(sketch, "E15.23", {"start": v(286.4, -29.63) * mm, "end": v(282.76, -28.18) * mm});
            skLineSegment(sketch, "E15.24", {"start": v(282.76, -28.18) * mm, "end": v(279.34, -26.28) * mm});
            skLineSegment(sketch, "E15.25", {"start": v(279.34, -26.28) * mm, "end": v(276.18, -23.98) * mm});
            skLineSegment(sketch, "E15.26", {"start": v(276.18, -23.98) * mm, "end": v(273.33, -21.29) * mm});
            skLineSegment(sketch, "E15.27", {"start": v(273.33, -21.29) * mm, "end": v(270.84, -18.26) * mm});
            skLineSegment(sketch, "E15.28", {"start": v(270.84, -18.26) * mm, "end": v(268.75, -14.95) * mm});
            skLineSegment(sketch, "E15.29", {"start": v(268.75, -14.95) * mm, "end": v(267.1, -11.4) * mm});
            skLineSegment(sketch, "E15.30", {"start": v(267.1, -11.4) * mm, "end": v(265.9, -7.68) * mm});
            skLineSegment(sketch, "E15.31", {"start": v(265.9, -7.68) * mm, "end": v(265.17, -3.83) * mm});
            skLineSegment(sketch, "E15.32", {"start": v(265.17, -3.83) * mm, "end": v(264.93, 0.08) * mm});
            skLineSegment(sketch, "E15.33", {"start": v(264.93, 0.08) * mm, "end": v(265.19, 3.99) * mm});
            skLineSegment(sketch, "E15.34", {"start": v(265.19, 3.99) * mm, "end": v(265.93, 7.83) * mm});
            skLineSegment(sketch, "E15.35", {"start": v(265.93, 7.83) * mm, "end": v(267.15, 11.55) * mm});
            skLineSegment(sketch, "E15.36", {"start": v(267.15, 11.55) * mm, "end": v(268.83, 15.1) * mm});
            skLineSegment(sketch, "E15.37", {"start": v(268.83, 15.1) * mm, "end": v(270.93, 18.4) * mm});
            skLineSegment(sketch, "E15.38", {"start": v(270.93, 18.4) * mm, "end": v(273.44, 21.4) * mm});
            skLineSegment(sketch, "E15.39", {"start": v(273.44, 21.4) * mm, "end": v(276.3, 24.08) * mm});
            skLineSegment(sketch, "E15.40", {"start": v(276.3, 24.08) * mm, "end": v(279.47, 26.37) * mm});
            skLineSegment(sketch, "E15.41", {"start": v(279.47, 26.37) * mm, "end": v(282.9, 28.25) * mm});
            skLineSegment(sketch, "E15.42", {"start": v(282.9, 28.25) * mm, "end": v(286.55, 29.68) * mm});
            skLineSegment(sketch, "E15.43", {"start": v(286.55, 29.68) * mm, "end": v(290.35, 30.64) * mm});
            skLineSegment(sketch, "E15.44", {"start": v(290.35, 30.64) * mm, "end": v(294.23, 31.12) * mm});
            skLineSegment(sketch, "E15.45", {"start": v(294.23, 31.12) * mm, "end": v(298.15, 31.11) * mm});
            skLineSegment(sketch, "E15.46", {"start": v(298.15, 31.11) * mm, "end": v(302.03, 30.61) * mm});
            skLineSegment(sketch, "E15.47", {"start": v(302.03, 30.61) * mm, "end": v(305.82, 29.63) * mm});
            skLineSegment(sketch, "E15.48", {"start": v(305.82, 29.63) * mm, "end": v(309.46, 28.18) * mm});
            skLineSegment(sketch, "E15.49", {"start": v(309.46, 28.18) * mm, "end": v(312.89, 26.28) * mm});
            skPoint(sketch, "E15.0.midPoint", {"position": v(314.47, 25.13) * mm});
            skSolve(sketch);
        }
        {
            var Q0;
            Q0 = qSketchRegion(id + "F18", true);
            extrude(context, id + "F19", {"entities" : qUnion([Q0]), "operationType" : NewBodyOperationType.ADD, "oppositeDirection" : true, "depth" : 269.24 * mm});
        }
        {
            var Q0;
            Q0=qCreatedBy(makeId("Front.planeOp"),FACE);
            var sketch = newSketch(context, id + "F20", { "sketchPlane" : qUnion([Q0])});
            skCircle(sketch, "E16.cCircle", {"center": v(0, 246.53) * mm, "radius": 33.26 * mm, "construction": true});
            skLineSegment(sketch, "E16.0", {"start": v(33.26, 248.62) * mm, "end": v(33.26, 244.44) * mm});
            skLineSegment(sketch, "E16.1", {"start": v(33.26, 244.44) * mm, "end": v(32.73, 240.28) * mm});
            skLineSegment(sketch, "E16.2", {"start": v(32.73, 240.28) * mm, "end": v(31.7, 236.23) * mm});
            skLineSegment(sketch, "E16.3", {"start": v(31.7, 236.23) * mm, "end": v(30.15, 232.34) * mm});
            skLineSegment(sketch, "E16.4", {"start": v(30.15, 232.34) * mm, "end": v(28.13, 228.67) * mm});
            skLineSegment(sketch, "E16.5", {"start": v(28.13, 228.67) * mm, "end": v(25.67, 225.29) * mm});
            skLineSegment(sketch, "E16.6", {"start": v(25.67, 225.29) * mm, "end": v(22.81, 222.24) * mm});
            skLineSegment(sketch, "E16.7", {"start": v(22.81, 222.24) * mm, "end": v(19.59, 219.57) * mm});
            skLineSegment(sketch, "E16.8", {"start": v(19.59, 219.57) * mm, "end": v(16.05, 217.33) * mm});
            skLineSegment(sketch, "E16.9", {"start": v(16.05, 217.33) * mm, "end": v(12.27, 215.55) * mm});
            skLineSegment(sketch, "E16.10", {"start": v(12.27, 215.55) * mm, "end": v(8.29, 214.25) * mm});
            skLineSegment(sketch, "E16.11", {"start": v(8.29, 214.25) * mm, "end": v(4.18, 213.47) * mm});
            skLineSegment(sketch, "E16.12", {"start": v(4.18, 213.47) * mm, "end": v(0, 213.2) * mm});
            skLineSegment(sketch, "E16.13", {"start": v(0, 213.2) * mm, "end": v(-4.18, 213.47) * mm});
            skLineSegment(sketch, "E16.14", {"start": v(-4.18, 213.47) * mm, "end": v(-8.29, 214.25) * mm});
            skLineSegment(sketch, "E16.15", {"start": v(-8.29, 214.25) * mm, "end": v(-12.27, 215.55) * mm});
            skLineSegment(sketch, "E16.16", {"start": v(-12.27, 215.55) * mm, "end": v(-16.05, 217.33) * mm});
            skLineSegment(sketch, "E16.17", {"start": v(-16.05, 217.33) * mm, "end": v(-19.59, 219.57) * mm});
            skLineSegment(sketch, "E16.18", {"start": v(-19.59, 219.57) * mm, "end": v(-22.81, 222.24) * mm});
            skLineSegment(sketch, "E16.19", {"start": v(-22.81, 222.24) * mm, "end": v(-25.67, 225.29) * mm});
            skLineSegment(sketch, "E16.20", {"start": v(-25.67, 225.29) * mm, "end": v(-28.13, 228.67) * mm});
            skLineSegment(sketch, "E16.21", {"start": v(-28.13, 228.67) * mm, "end": v(-30.15, 232.34) * mm});
            skLineSegment(sketch, "E16.22", {"start": v(-30.15, 232.34) * mm, "end": v(-31.7, 236.23) * mm});
            skLineSegment(sketch, "E16.23", {"start": v(-31.7, 236.23) * mm, "end": v(-32.73, 240.28) * mm});
            skLineSegment(sketch, "E16.24", {"start": v(-32.73, 240.28) * mm, "end": v(-33.26, 244.44) * mm});
            skLineSegment(sketch, "E16.25", {"start": v(-33.26, 244.44) * mm, "end": v(-33.26, 248.62) * mm});
            skLineSegment(sketch, "E16.26", {"start": v(-33.26, 248.62) * mm, "end": v(-32.73, 252.77) * mm});
            skLineSegment(sketch, "E16.27", {"start": v(-32.73, 252.77) * mm, "end": v(-31.7, 256.83) * mm});
            skLineSegment(sketch, "E16.28", {"start": v(-31.7, 256.83) * mm, "end": v(-30.15, 260.72) * mm});
            skLineSegment(sketch, "E16.29", {"start": v(-30.15, 260.72) * mm, "end": v(-28.13, 264.38) * mm});
            skLineSegment(sketch, "E16.30", {"start": v(-28.13, 264.38) * mm, "end": v(-25.67, 267.77) * mm});
            skLineSegment(sketch, "E16.31", {"start": v(-25.67, 267.77) * mm, "end": v(-22.81, 270.82) * mm});
            skLineSegment(sketch, "E16.32", {"start": v(-22.81, 270.82) * mm, "end": v(-19.59, 273.49) * mm});
            skLineSegment(sketch, "E16.33", {"start": v(-19.59, 273.49) * mm, "end": v(-16.05, 275.73) * mm});
            skLineSegment(sketch, "E16.34", {"start": v(-16.05, 275.73) * mm, "end": v(-12.27, 277.51) * mm});
            skLineSegment(sketch, "E16.35", {"start": v(-12.27, 277.51) * mm, "end": v(-8.29, 278.8) * mm});
            skLineSegment(sketch, "E16.36", {"start": v(-8.29, 278.8) * mm, "end": v(-4.18, 279.59) * mm});
            skLineSegment(sketch, "E16.37", {"start": v(-4.18, 279.59) * mm, "end": v(0, 279.85) * mm});
            skLineSegment(sketch, "E16.38", {"start": v(0, 279.85) * mm, "end": v(4.18, 279.59) * mm});
            skLineSegment(sketch, "E16.39", {"start": v(4.18, 279.59) * mm, "end": v(8.29, 278.8) * mm});
            skLineSegment(sketch, "E16.40", {"start": v(8.29, 278.8) * mm, "end": v(12.27, 277.51) * mm});
            skLineSegment(sketch, "E16.41", {"start": v(12.27, 277.51) * mm, "end": v(16.05, 275.73) * mm});
            skLineSegment(sketch, "E16.42", {"start": v(16.05, 275.73) * mm, "end": v(19.59, 273.49) * mm});
            skLineSegment(sketch, "E16.43", {"start": v(19.59, 273.49) * mm, "end": v(22.81, 270.82) * mm});
            skLineSegment(sketch, "E16.44", {"start": v(22.81, 270.82) * mm, "end": v(25.67, 267.77) * mm});
            skLineSegment(sketch, "E16.45", {"start": v(25.67, 267.77) * mm, "end": v(28.13, 264.38) * mm});
            skLineSegment(sketch, "E16.46", {"start": v(28.13, 264.38) * mm, "end": v(30.15, 260.72) * mm});
            skLineSegment(sketch, "E16.47", {"start": v(30.15, 260.72) * mm, "end": v(31.7, 256.83) * mm});
            skLineSegment(sketch, "E16.48", {"start": v(31.7, 256.83) * mm, "end": v(32.73, 252.77) * mm});
            skLineSegment(sketch, "E16.49", {"start": v(32.73, 252.77) * mm, "end": v(33.26, 248.62) * mm});
            skPoint(sketch, "E16.0.midPoint", {"position": v(33.26, 246.53) * mm});
            skSolve(sketch);
        }
        {
            var Q0;
            Q0 = qSketchRegion(id + "F20", true);
            extrude(context, id + "F21", {"entities" : qUnion([Q0]), "operationType" : NewBodyOperationType.ADD, "oppositeDirection" : true, "depth" : 269.24 * mm});
        }
        {
            var Q0;
            Q0=qCreatedBy(makeId("Front.planeOp"),FACE);
            var sketch = newSketch(context, id + "F22", { "sketchPlane" : qUnion([Q0])});
            skCircle(sketch, "E17.cCircle", {"center": v(-286.67, 0) * mm, "radius": 32.82 * mm, "construction": true});
            skLineSegment(sketch, "E17.0", {"start": v(-304.07, 27.9) * mm, "end": v(-300.44, 29.86) * mm});
            skLineSegment(sketch, "E17.1", {"start": v(-300.44, 29.86) * mm, "end": v(-296.59, 31.35) * mm});
            skLineSegment(sketch, "E17.2", {"start": v(-296.59, 31.35) * mm, "end": v(-292.58, 32.35) * mm});
            skLineSegment(sketch, "E17.3", {"start": v(-292.58, 32.35) * mm, "end": v(-288.48, 32.83) * mm});
            skLineSegment(sketch, "E17.4", {"start": v(-288.48, 32.83) * mm, "end": v(-284.35, 32.8) * mm});
            skLineSegment(sketch, "E17.5", {"start": v(-284.35, 32.8) * mm, "end": v(-280.25, 32.25) * mm});
            skLineSegment(sketch, "E17.6", {"start": v(-280.25, 32.25) * mm, "end": v(-276.26, 31.2) * mm});
            skLineSegment(sketch, "E17.7", {"start": v(-276.26, 31.2) * mm, "end": v(-272.43, 29.64) * mm});
            skLineSegment(sketch, "E17.8", {"start": v(-272.43, 29.64) * mm, "end": v(-268.83, 27.63) * mm});
            skLineSegment(sketch, "E17.9", {"start": v(-268.83, 27.63) * mm, "end": v(-265.5, 25.17) * mm});
            skLineSegment(sketch, "E17.10", {"start": v(-265.5, 25.17) * mm, "end": v(-262.52, 22.32) * mm});
            skLineSegment(sketch, "E17.11", {"start": v(-262.52, 22.32) * mm, "end": v(-259.91, 19.12) * mm});
            skLineSegment(sketch, "E17.12", {"start": v(-259.91, 19.12) * mm, "end": v(-257.73, 15.62) * mm});
            skLineSegment(sketch, "E17.13", {"start": v(-257.73, 15.62) * mm, "end": v(-256, 11.87) * mm});
            skLineSegment(sketch, "E17.14", {"start": v(-256, 11.87) * mm, "end": v(-254.75, 7.93) * mm});
            skLineSegment(sketch, "E17.15", {"start": v(-254.75, 7.93) * mm, "end": v(-254.01, 3.87) * mm});
            skLineSegment(sketch, "E17.16", {"start": v(-254.01, 3.87) * mm, "end": v(-253.78, -0.26) * mm});
            skLineSegment(sketch, "E17.17", {"start": v(-253.78, -0.26) * mm, "end": v(-254.08, -4.38) * mm});
            skLineSegment(sketch, "E17.18", {"start": v(-254.08, -4.38) * mm, "end": v(-254.88, -8.43) * mm});
            skLineSegment(sketch, "E17.19", {"start": v(-254.88, -8.43) * mm, "end": v(-256.19, -12.34) * mm});
            skLineSegment(sketch, "E17.20", {"start": v(-256.19, -12.34) * mm, "end": v(-257.98, -16.07) * mm});
            skLineSegment(sketch, "E17.21", {"start": v(-257.98, -16.07) * mm, "end": v(-260.22, -19.54) * mm});
            skLineSegment(sketch, "E17.22", {"start": v(-260.22, -19.54) * mm, "end": v(-262.87, -22.7) * mm});
            skLineSegment(sketch, "E17.23", {"start": v(-262.87, -22.7) * mm, "end": v(-265.9, -25.5) * mm});
            skLineSegment(sketch, "E17.24", {"start": v(-265.9, -25.5) * mm, "end": v(-269.26, -27.9) * mm});
            skLineSegment(sketch, "E17.25", {"start": v(-269.26, -27.9) * mm, "end": v(-272.9, -29.86) * mm});
            skLineSegment(sketch, "E17.26", {"start": v(-272.9, -29.86) * mm, "end": v(-276.75, -31.35) * mm});
            skLineSegment(sketch, "E17.27", {"start": v(-276.75, -31.35) * mm, "end": v(-280.76, -32.35) * mm});
            skLineSegment(sketch, "E17.28", {"start": v(-280.76, -32.35) * mm, "end": v(-284.86, -32.83) * mm});
            skLineSegment(sketch, "E17.29", {"start": v(-284.86, -32.83) * mm, "end": v(-288.99, -32.8) * mm});
            skLineSegment(sketch, "E17.30", {"start": v(-288.99, -32.8) * mm, "end": v(-293.08, -32.25) * mm});
            skLineSegment(sketch, "E17.31", {"start": v(-293.08, -32.25) * mm, "end": v(-297.07, -31.2) * mm});
            skLineSegment(sketch, "E17.32", {"start": v(-297.07, -31.2) * mm, "end": v(-300.9, -29.64) * mm});
            skLineSegment(sketch, "E17.33", {"start": v(-300.9, -29.64) * mm, "end": v(-304.5, -27.63) * mm});
            skLineSegment(sketch, "E17.34", {"start": v(-304.5, -27.63) * mm, "end": v(-307.83, -25.17) * mm});
            skLineSegment(sketch, "E17.35", {"start": v(-307.83, -25.17) * mm, "end": v(-310.81, -22.32) * mm});
            skLineSegment(sketch, "E17.36", {"start": v(-310.81, -22.32) * mm, "end": v(-313.42, -19.12) * mm});
            skLineSegment(sketch, "E17.37", {"start": v(-313.42, -19.12) * mm, "end": v(-315.6, -15.62) * mm});
            skLineSegment(sketch, "E17.38", {"start": v(-315.6, -15.62) * mm, "end": v(-317.34, -11.87) * mm});
            skLineSegment(sketch, "E17.39", {"start": v(-317.34, -11.87) * mm, "end": v(-318.58, -7.93) * mm});
            skLineSegment(sketch, "E17.40", {"start": v(-318.58, -7.93) * mm, "end": v(-319.32, -3.87) * mm});
            skLineSegment(sketch, "E17.41", {"start": v(-319.32, -3.87) * mm, "end": v(-319.55, 0.26) * mm});
            skLineSegment(sketch, "E17.42", {"start": v(-319.55, 0.26) * mm, "end": v(-319.26, 4.38) * mm});
            skLineSegment(sketch, "E17.43", {"start": v(-319.26, 4.38) * mm, "end": v(-318.45, 8.43) * mm});
            skLineSegment(sketch, "E17.44", {"start": v(-318.45, 8.43) * mm, "end": v(-317.15, 12.34) * mm});
            skLineSegment(sketch, "E17.45", {"start": v(-317.15, 12.34) * mm, "end": v(-315.36, 16.07) * mm});
            skLineSegment(sketch, "E17.46", {"start": v(-315.36, 16.07) * mm, "end": v(-313.12, 19.54) * mm});
            skLineSegment(sketch, "E17.47", {"start": v(-313.12, 19.54) * mm, "end": v(-310.46, 22.7) * mm});
            skLineSegment(sketch, "E17.48", {"start": v(-310.46, 22.7) * mm, "end": v(-307.43, 25.5) * mm});
            skLineSegment(sketch, "E17.49", {"start": v(-307.43, 25.5) * mm, "end": v(-304.07, 27.9) * mm});
            skPoint(sketch, "E17.0.midPoint", {"position": v(-302.25, 28.88) * mm});
            skSolve(sketch);
        }
        {
            var Q0;
            Q0 = qSketchRegion(id + "F22", true);
            extrude(context, id + "F23", {"entities" : qUnion([Q0]), "operationType" : NewBodyOperationType.ADD, "oppositeDirection" : true, "depth" : 269.24 * mm});
        }
        {
            var Q0;
            Q0=qCreatedBy(makeId("Front.planeOp"),FACE);
            var sketch = newSketch(context, id + "F24", { "sketchPlane" : qUnion([Q0])});
            skCircle(sketch, "E18.cCircle", {"center": v(0, -234.67) * mm, "radius": 32.59 * mm, "construction": true});
            skLineSegment(sketch, "E18.0", {"start": v(-2.05, -202.08) * mm, "end": v(2.05, -202.08) * mm});
            skLineSegment(sketch, "E18.1", {"start": v(2.05, -202.08) * mm, "end": v(6.12, -202.6) * mm});
            skLineSegment(sketch, "E18.2", {"start": v(6.12, -202.6) * mm, "end": v(10.1, -203.6) * mm});
            skLineSegment(sketch, "E18.3", {"start": v(10.1, -203.6) * mm, "end": v(13.9, -205.12) * mm});
            skLineSegment(sketch, "E18.4", {"start": v(13.9, -205.12) * mm, "end": v(17.5, -207.1) * mm});
            skLineSegment(sketch, "E18.5", {"start": v(17.5, -207.1) * mm, "end": v(20.81, -209.5) * mm});
            skLineSegment(sketch, "E18.6", {"start": v(20.81, -209.5) * mm, "end": v(23.8, -212.31) * mm});
            skLineSegment(sketch, "E18.7", {"start": v(23.8, -212.31) * mm, "end": v(26.42, -215.47) * mm});
            skLineSegment(sketch, "E18.8", {"start": v(26.42, -215.47) * mm, "end": v(28.61, -218.93) * mm});
            skLineSegment(sketch, "E18.9", {"start": v(28.61, -218.93) * mm, "end": v(30.36, -222.64) * mm});
            skLineSegment(sketch, "E18.10", {"start": v(30.36, -222.64) * mm, "end": v(31.63, -226.54) * mm});
            skLineSegment(sketch, "E18.11", {"start": v(31.63, -226.54) * mm, "end": v(32.4, -230.57) * mm});
            skLineSegment(sketch, "E18.12", {"start": v(32.4, -230.57) * mm, "end": v(32.65, -234.67) * mm});
            skLineSegment(sketch, "E18.13", {"start": v(32.65, -234.67) * mm, "end": v(32.4, -238.76) * mm});
            skLineSegment(sketch, "E18.14", {"start": v(32.4, -238.76) * mm, "end": v(31.63, -242.79) * mm});
            skLineSegment(sketch, "E18.15", {"start": v(31.63, -242.79) * mm, "end": v(30.36, -246.69) * mm});
            skLineSegment(sketch, "E18.16", {"start": v(30.36, -246.69) * mm, "end": v(28.61, -250.4) * mm});
            skLineSegment(sketch, "E18.17", {"start": v(28.61, -250.4) * mm, "end": v(26.42, -253.86) * mm});
            skLineSegment(sketch, "E18.18", {"start": v(26.42, -253.86) * mm, "end": v(23.8, -257.02) * mm});
            skLineSegment(sketch, "E18.19", {"start": v(23.8, -257.02) * mm, "end": v(20.81, -259.83) * mm});
            skLineSegment(sketch, "E18.20", {"start": v(20.81, -259.83) * mm, "end": v(17.5, -262.24) * mm});
            skLineSegment(sketch, "E18.21", {"start": v(17.5, -262.24) * mm, "end": v(13.9, -264.21) * mm});
            skLineSegment(sketch, "E18.22", {"start": v(13.9, -264.21) * mm, "end": v(10.1, -265.72) * mm});
            skLineSegment(sketch, "E18.23", {"start": v(10.1, -265.72) * mm, "end": v(6.12, -266.74) * mm});
            skLineSegment(sketch, "E18.24", {"start": v(6.12, -266.74) * mm, "end": v(2.05, -267.25) * mm});
            skLineSegment(sketch, "E18.25", {"start": v(2.05, -267.25) * mm, "end": v(-2.05, -267.25) * mm});
            skLineSegment(sketch, "E18.26", {"start": v(-2.05, -267.25) * mm, "end": v(-6.12, -266.74) * mm});
            skLineSegment(sketch, "E18.27", {"start": v(-6.12, -266.74) * mm, "end": v(-10.1, -265.72) * mm});
            skLineSegment(sketch, "E18.28", {"start": v(-10.1, -265.72) * mm, "end": v(-13.9, -264.21) * mm});
            skLineSegment(sketch, "E18.29", {"start": v(-13.9, -264.21) * mm, "end": v(-17.5, -262.24) * mm});
            skLineSegment(sketch, "E18.30", {"start": v(-17.5, -262.24) * mm, "end": v(-20.81, -259.83) * mm});
            skLineSegment(sketch, "E18.31", {"start": v(-20.81, -259.83) * mm, "end": v(-23.8, -257.02) * mm});
            skLineSegment(sketch, "E18.32", {"start": v(-23.8, -257.02) * mm, "end": v(-26.42, -253.86) * mm});
            skLineSegment(sketch, "E18.33", {"start": v(-26.42, -253.86) * mm, "end": v(-28.61, -250.4) * mm});
            skLineSegment(sketch, "E18.34", {"start": v(-28.61, -250.4) * mm, "end": v(-30.36, -246.69) * mm});
            skLineSegment(sketch, "E18.35", {"start": v(-30.36, -246.69) * mm, "end": v(-31.63, -242.79) * mm});
            skLineSegment(sketch, "E18.36", {"start": v(-31.63, -242.79) * mm, "end": v(-32.4, -238.76) * mm});
            skLineSegment(sketch, "E18.37", {"start": v(-32.4, -238.76) * mm, "end": v(-32.65, -234.67) * mm});
            skLineSegment(sketch, "E18.38", {"start": v(-32.65, -234.67) * mm, "end": v(-32.4, -230.57) * mm});
            skLineSegment(sketch, "E18.39", {"start": v(-32.4, -230.57) * mm, "end": v(-31.63, -226.54) * mm});
            skLineSegment(sketch, "E18.40", {"start": v(-31.63, -226.54) * mm, "end": v(-30.36, -222.64) * mm});
            skLineSegment(sketch, "E18.41", {"start": v(-30.36, -222.64) * mm, "end": v(-28.61, -218.93) * mm});
            skLineSegment(sketch, "E18.42", {"start": v(-28.61, -218.93) * mm, "end": v(-26.42, -215.47) * mm});
            skLineSegment(sketch, "E18.43", {"start": v(-26.42, -215.47) * mm, "end": v(-23.8, -212.31) * mm});
            skLineSegment(sketch, "E18.44", {"start": v(-23.8, -212.31) * mm, "end": v(-20.81, -209.5) * mm});
            skLineSegment(sketch, "E18.45", {"start": v(-20.81, -209.5) * mm, "end": v(-17.5, -207.1) * mm});
            skLineSegment(sketch, "E18.46", {"start": v(-17.5, -207.1) * mm, "end": v(-13.9, -205.12) * mm});
            skLineSegment(sketch, "E18.47", {"start": v(-13.9, -205.12) * mm, "end": v(-10.1, -203.6) * mm});
            skLineSegment(sketch, "E18.48", {"start": v(-10.1, -203.6) * mm, "end": v(-6.12, -202.6) * mm});
            skLineSegment(sketch, "E18.49", {"start": v(-6.12, -202.6) * mm, "end": v(-2.05, -202.08) * mm});
            skPoint(sketch, "E18.0.midPoint", {"position": v(0, -202.08) * mm});
            skSolve(sketch);
        }
        {
            var Q0;
            Q0 = qSketchRegion(id + "F24", true);
            extrude(context, id + "F25", {"entities" : qUnion([Q0]), "operationType" : NewBodyOperationType.ADD, "oppositeDirection" : true, "depth" : 269.24 * mm});
        }
    });
